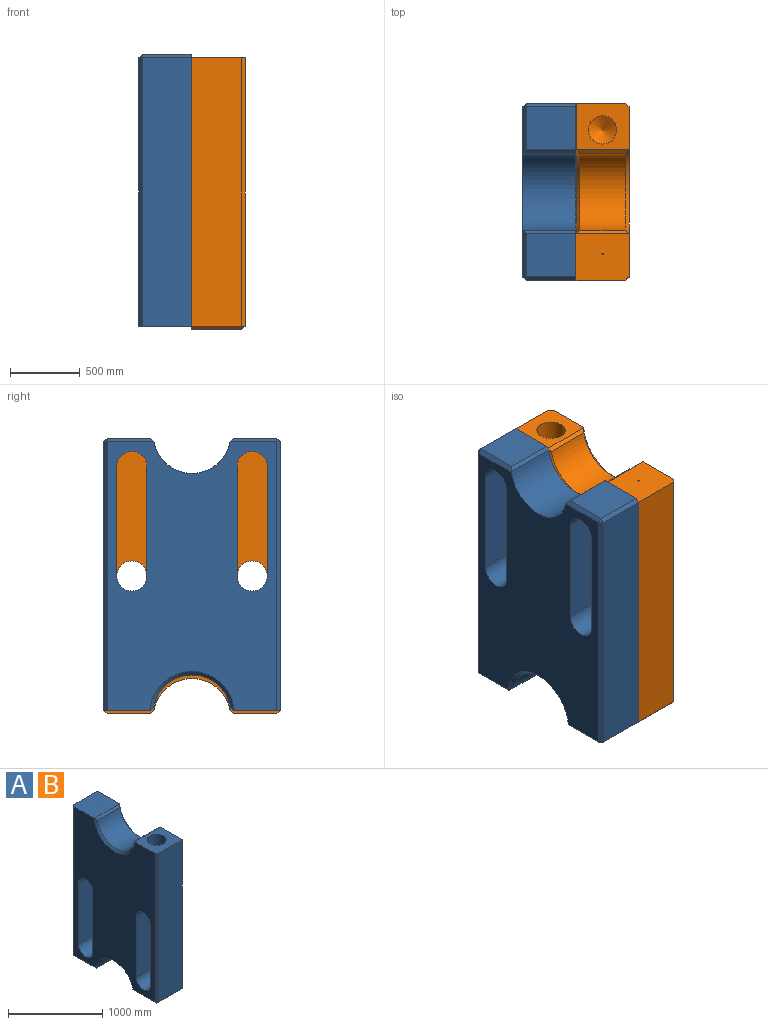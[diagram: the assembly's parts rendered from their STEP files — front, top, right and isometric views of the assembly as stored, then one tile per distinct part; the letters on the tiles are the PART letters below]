
ASSEMBLY  parts=2 mates=1
PART A: 36 faces, bbox 381x1270x1957.9 mm
  f0: cylinder r=107.95mm len=381mm, axis (-1,0,0), area 129210.4mm2, adj f1,f15,f16,f17
  f1: plane 787.4x381mm, normal (0,1,0), area 299999.4mm2, adj f0,f2,f16,f17
  f2: cylinder r=107.95mm len=381mm, axis (-1,0,0), area 129210.4mm2, adj f1,f15,f16,f17
  f3: plane 381x334.46mm, normal (0,0,1), area 94668.4mm2, adj f4,f16,f17,f21,f22,f23,f24,f26
  f4: plane 1930.4x355.6mm, normal (0,-1,0), area 686450.2mm2, adj f3,f16,f26,f27
  f5: plane 355.6x309.06mm, normal (0,0,-1), area 109902.9mm2, adj f16,f27,f29,f30
  f6: cylinder r=279.4mm len=550.98mm, axis (-1,0,0), area 298758.6mm2, adj f16,f17,f29,f30,f34,f35
  f7: plane 355.6x309.06mm, normal (0,0,-1), area 109902.9mm2, adj f16,f31,f34,f35
  f8: plane 1930.4x355.6mm, normal (0,1,0), area 686450.2mm2, adj f9,f16,f31,f32
  f9: plane 381x334.46mm, normal (0,0,1), area 127034mm2, adj f8,f16,f17,f19,f23,f24,f25,f32
  f10: plane 787.4x381mm, normal (0,1,0), area 299999.4mm2, adj f11,f14,f16,f17
  f11: cylinder r=107.95mm len=381mm, axis (-1,0,0), area 129210.4mm2, adj f10,f12,f16,f17
  f12: plane 787.4x381mm, normal (0,-1,0), area 299999.4mm2, adj f11,f14,f16,f17
  f13: cylinder r=279.4mm len=550.98mm, axis (-1,0,0), area 258939.9mm2, adj f22,f23,f24,f25
  f14: cylinder r=107.95mm len=381mm, axis (-1,0,0), area 129210.4mm2, adj f10,f12,f16,f17
  f15: plane 787.4x381mm, normal (0,-1,0), area 299999.4mm2, adj f0,f2,f16,f17
  f16: plane 1955.8x1270mm, normal (1,0,0), area 1830621.1mm2, adj f0,f1,f2,f3,f4,f5,f6,f7
  f17: plane 1930.4x1219.2mm, normal (-1,0,0), area 1715465.9mm2, adj f0,f1,f2,f3,f6,f9,f10,f11
  f18: cone r=0mm half-angle=59deg, axis (0,0,1), area 74.2mm2, adj f19
  f19: cylinder r=4.5mm len=482.6mm, axis (0,0,1), area 13645.2mm2, adj f9,f18
  f20: cone r=0mm half-angle=59deg, axis (0,0,1), area 37833.1mm2, adj f21
  f21: cylinder r=101.6mm len=482.6mm, axis (0,0,1), area 308078.1mm2, adj f3,f20
  f22: plane 374.62x25.04mm, normal (0,0.65,0.76), area 11545mm2, adj f3,f13,f23,f24
  f23: cone r=279.4mm half-angle=45deg, axis (1,0,0), area 30477mm2, adj f3,f9,f13,f16,f22,f25
  f24: cone r=304.8mm half-angle=45deg, axis (-1,0,0), area 30477mm2, adj f3,f9,f13,f17,f22,f25
  f25: plane 374.62x25.04mm, normal (0,-0.65,0.76), area 11545mm2, adj f9,f13,f23,f24
  f26: plane 1930.4x25.4mm, normal (-0.71,-0.71,0), area 69341.9mm2, adj f3,f4,f17,f28
  f27: plane 355.6x25.4mm, normal (0,-0.71,-0.71), area 12773.5mm2, adj f4,f5,f16,f28
  f28: plane 25.4x25.4mm, normal (-0.58,-0.58,-0.58), area 558.7mm2, adj f26,f27,f29
  f29: plane 334.86x25.4mm, normal (-0.71,0,-0.71), area 11628.9mm2, adj f5,f6,f17,f28,f30
  f30: plane 376.77x25.04mm, normal (0,0.65,-0.76), area 12007.6mm2, adj f5,f6,f16,f29
  f31: plane 355.6x25.4mm, normal (0,0.71,-0.71), area 12773.5mm2, adj f7,f8,f16,f33
  f32: plane 1930.4x25.4mm, normal (-0.71,0.71,0), area 69341.9mm2, adj f8,f9,f17,f33
  f33: plane 25.4x25.4mm, normal (-0.58,0.58,-0.58), area 558.7mm2, adj f31,f32,f34
  f34: plane 334.86x25.4mm, normal (-0.71,0,-0.71), area 11628.9mm2, adj f6,f7,f17,f33,f35
  f35: plane 376.77x25.04mm, normal (0,-0.65,-0.76), area 12007.6mm2, adj f6,f7,f16,f34
PART B: same geometry as A
PLACE A rot(axis=(1,0,0),180deg) t=(465.58,19.14,2431.33)mm
PLACE B rot(axis=(0,0,-1),180deg) t=(1227.58,19.14,450.13)mm
MATE planar B.f16 <-> A.f16  axis (-1,0,0) through (846.58,350.4,2405.93)mm
